# Revit family: Lift Machine (gearless) 2
name_source: partatom
category: Generic Models
units: mm (PartAtom-declared; Revit-internal decimal feet)

## family parameters
Always vertical = Yes
Can host rebar = No
Cut with Voids When Loaded = No
Maintain Annotation Orientation = No
Part Type = Normal
Room Calculation Point = No
Round Connector Dimension = Use Diameter
Shared = No
Work Plane-Based = No

## types (1)
- Lift Machine (gearless) 2
    Base Width = 780 mm  [stored 2.55906 ft]
    Brake Height = 313 mm
    Brake Width = 172 mm
    BrakeType = Block
    Default Elevation = 0 mm  [stored 0 ft]
    DriveType = Traction
    Geared = gearless
    Machine Brake Model = BCA DD55 Brake
    Machine_RatedSpeed = 1.5 m/s
    Motor Length = 250 mm  [stored 0.82021 ft]
    Rope Guard = 50 mm  [stored 0.164042 ft]
    RopeCount = 6
    RopeDiameter = 10
    Rope_BreakingStrength = 350
    Rope_Configuration = single wrap
    Roping = 2
    Sheave diameter = 780 mm  [stored 2.55906 ft]
    Sheave width = 325 mm
    Type of Drive System = Traction
    cut width and height off bracket (1/8) = 180 mm  [stored 0.590551 ft]
    diameter of motor = 1040 mm  [stored 3.41207 ft]
    height of base = 70 mm  [stored 0.229659 ft]
    height of bracket = 1000 mm  [stored 3.28084 ft]
    inner diameter = 650 mm  [stored 2.13255 ft]
    sheave btm to base = 10 mm  [stored 0.0328084 ft]
    sheave inner diameter = 730 mm  [stored 2.39501 ft]
    width of bracket = 1260 mm  [stored 4.13386 ft]

note: [stored X ft] marks values corroborated as IEEE doubles in the binary element streams (Revit-internal decimal feet)

## geometry (parser evidence)
native form markers: Sweep x3
no freeform markers — native parametric forms only
